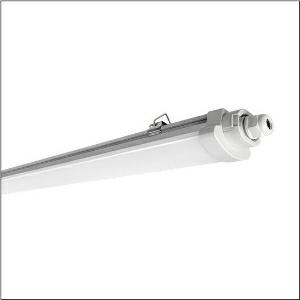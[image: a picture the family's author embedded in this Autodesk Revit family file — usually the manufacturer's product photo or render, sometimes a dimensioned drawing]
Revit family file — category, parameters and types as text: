
# Revit family: monsun_r__41_51fk20mn460a_a5b0
name_source: partatom
category: Lighting Fixtures
units: mm (PartAtom-declared; Revit-internal decimal feet)

## family parameters
Cut with Voids When Loaded = No
Host = Face
Light Source = No
Part Type = Normal
Room Calculation Point = No
Round Connector Dimension = Use Diameter
Shared = No

## types (1)
- --- (1 x LED, 6000 lm, 46 W, 4000K)
    Apparent Load = 46 VA
    CIE Flux Codes = 44 74 91 91 100
    Color Rendering = 80
    Color Temperature = 4000K
    Default Elevation = 1800 mm
    Description = Monsun® 41, damp-proof luminaire, primary optical cover: diffuser, of PC, frosted, light emission: direct distribution, primary light characteristic: symmetric, installation type: suspended mounting, surface-mounted, LED, rated luminous flux: 6.000lm, luminous efficacy: 130lm/W, light colour: 840, colour temperature: 4000K, control gear: ON/OFF Multilumen, with terminal, 3-pole, mains connection: 220..240V, AC, 50/60Hz, rated input power: 46W, housing, luminaire housing, of PC, grey, length: 1.500mm, width: 79mm, height: 52mm, end cap, of PC, grey, ceiling mounting element, of stainless steel (V2A), protection rating (complete): IP65, insulation class (complete): insulation class II (safety insulation), certification: CE, UKCA, protection symbol: D, impact resistance: IK08, permissible operating ambient temperature: -20..+35°C, corresponds to IFS (International Featured Standards) requirements for safety and quality in the food industry, contact your sales advisor before using the luminaires in applications with unclear chemical exposure, large temperature fluctuations or condensation-forming humidity, packaging unit: 1 piece
    Height = 54 mm
    Lamp = 1 x LED
    Lamp Light Flux = 6000 lm
    Lamp Power = 46 W
    Lamp count = 1
    Length = 1500 mm
    Luminous efficacy = 130 lm/W
    Manufacturer = Siteco
    ModVariant = No
    Model = 51FK20MN460A
    Mounting Place = Ceiling
    Mounting Type = Surface mounted
    Number of Poles = 1
    OnlyDefault = Yes
    Power Factor = 1
    Product Name = Monsun® 41
    Product group = damp-proof luminaire
    ProductGroupID = 300
    Protection Class = Protection class II
    Protection Degree = IP 65
    RLX_Detail_Level = 1
    RLX_Emergency_Light_Flux = 0 lm
    RLX_Emergency_Type = 0
    RLX_Emergency_Type_DB = No
    RlxData = <blob elided: 28861 chars, md5=3097d5c3>
    Socket = socket
    Standby Power = 0 W
    System Light Flux = 6000 lm
    System Power = 46 W
    Type Comments = factory setting: luminous flux: 100 % | (HIGH)
    Type Image = l_1007037.jpg
    URL = http://relux.com
    VarID = @adj_174694
    Voltage = 0 V
    Weight = 0.00 kg
    Width = 79 mm

## geometry (parser evidence)
native form markers: Blend x4, Sweep x11
no freeform markers — native parametric forms only
